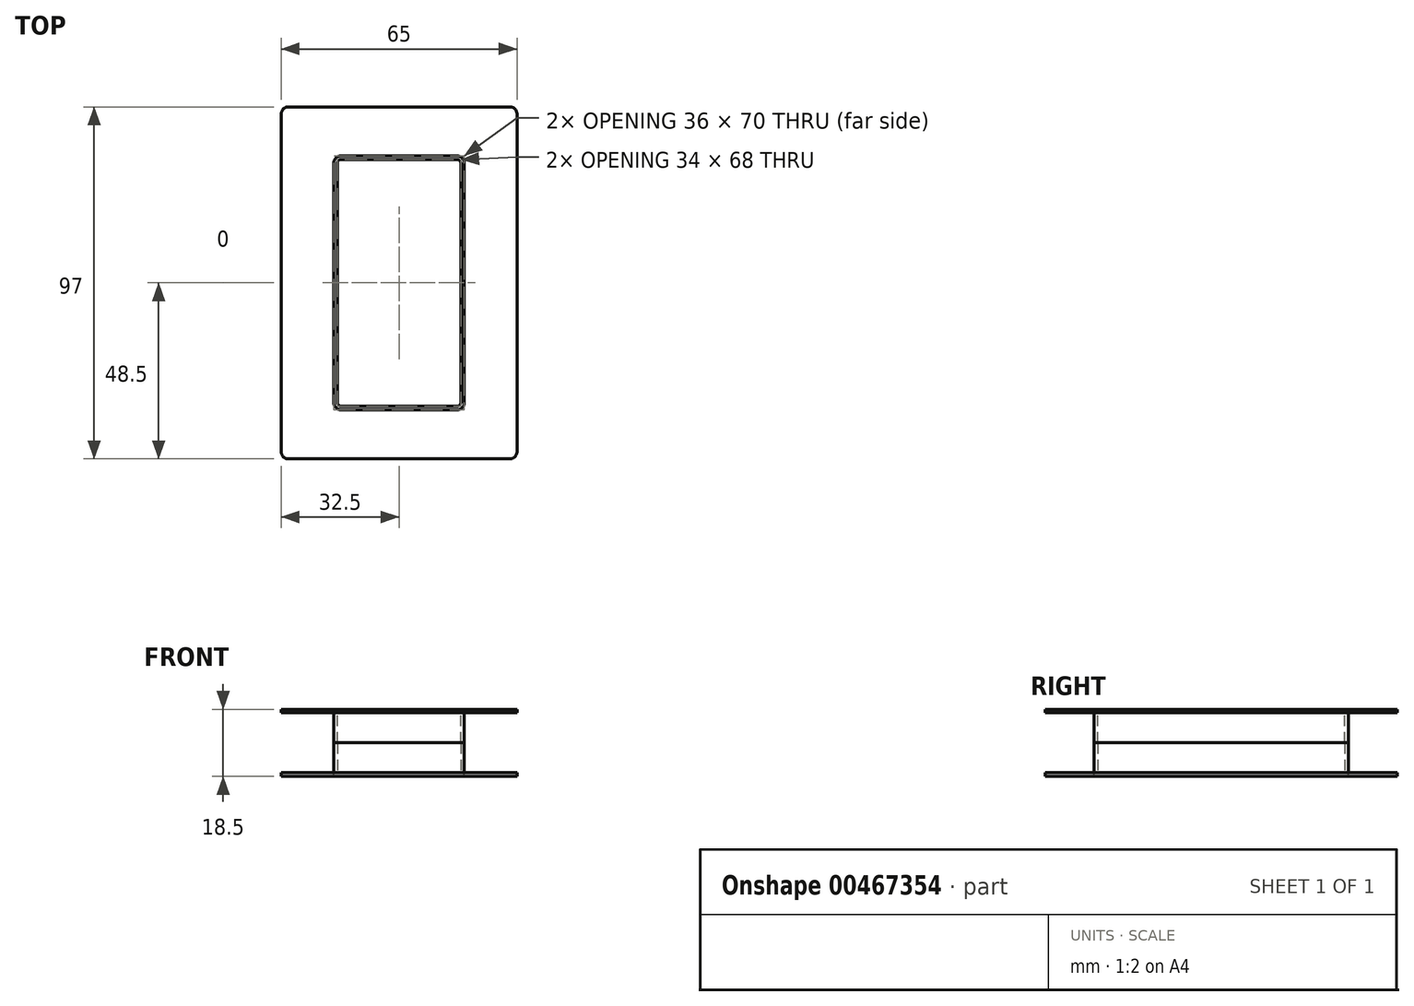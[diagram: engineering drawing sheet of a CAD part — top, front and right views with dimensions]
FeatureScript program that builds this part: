
annotation { "Feature Type Name" : "Feature", "Feature Type Description" : "" }
export const myFeature = defineFeature(function(context is Context, id is Id, definition is map)
    precondition{}
    {
        {
            var Q0;
            Q0=qCreatedBy(makeId("Top.planeOp"),FACE);
            var sketch = newSketch(context, id + "F0", { "sketchPlane" : qUnion([Q0])});
            skLineSegment(sketch, "E0.bottom", {"start": v(-16, -33) * mm, "end": v(16, -33) * mm, "construction": true});
            skLineSegment(sketch, "E0.top", {"start": v(-16, 33) * mm, "end": v(16, 33) * mm, "construction": true});
            skLineSegment(sketch, "E0.left", {"start": v(-16, -33) * mm, "end": v(-16, 33) * mm, "construction": true});
            skLineSegment(sketch, "E0.right", {"start": v(16, -33) * mm, "end": v(16, 33) * mm, "construction": true});
            skPoint(sketch, "E0.middle", {"position": v(0, 0) * mm});
            skLineSegment(sketch, "E1.bottom", {"start": v(33, -33) * mm, "end": v(65, -33) * mm, "construction": true});
            skLineSegment(sketch, "E1.top", {"start": v(33, 33) * mm, "end": v(65, 33) * mm, "construction": true});
            skLineSegment(sketch, "E1.left", {"start": v(33, -33) * mm, "end": v(33, 33) * mm, "construction": true});
            skLineSegment(sketch, "E1.right", {"start": v(65, -33) * mm, "end": v(65, 33) * mm, "construction": true});
            skLineSegment(sketch, "E2", {"start": v(33, 33) * mm, "end": v(16, 33) * mm, "construction": true});
            skLineSegment(sketch, "E3.MirrorCS", {"start": v(-33, 33) * mm, "end": v(-65, 33) * mm, "construction": true});
            skLineSegment(sketch, "E4.MirrorCS", {"start": v(-33, -33) * mm, "end": v(-65, -33) * mm, "construction": true});
            skLineSegment(sketch, "E5.MirrorCS", {"start": v(-33, -33) * mm, "end": v(-33, 33) * mm, "construction": true});
            skLineSegment(sketch, "E6.MirrorCS", {"start": v(-65, -33) * mm, "end": v(-65, 33) * mm, "construction": true});
            skArc(sketch, "E7", {"start": v(17, 33) * mm, "mid": v(16.7, 33.7) * mm, "end": v(16, 34) * mm});
            skArc(sketch, "E8.MirrorCS", {"start": v(-17, 33) * mm, "mid": v(-16.7, 33.7) * mm, "end": v(-16, 34) * mm});
            skArc(sketch, "E9.MirrorCS", {"start": v(-17, -33) * mm, "mid": v(-16.7, -33.7) * mm, "end": v(-16, -34) * mm});
            skArc(sketch, "E10.MirrorCS", {"start": v(17, -33) * mm, "mid": v(16.7, -33.7) * mm, "end": v(16, -34) * mm});
            skLineSegment(sketch, "E11", {"start": v(-16, 34) * mm, "end": v(16, 34) * mm});
            skLineSegment(sketch, "E12", {"start": v(17, 33) * mm, "end": v(17, -33) * mm});
            skLineSegment(sketch, "E13", {"start": v(16, -34) * mm, "end": v(-16, -34) * mm});
            skLineSegment(sketch, "E14", {"start": v(-17, -33) * mm, "end": v(-17, 33) * mm});
            skLineSegment(sketch, "E15", {"start": v(33, 0) * mm, "end": v(32.5, 0) * mm, "construction": true});
            skPoint(sketch, "E15.endSnap0", {"position": v(33, 0) * mm});
            skLineSegment(sketch, "E16", {"start": v(32.5, 0) * mm, "end": v(32.5, 46.5) * mm});
            skLineSegment(sketch, "E17.MirrorCS", {"start": v(32.5, 0) * mm, "end": v(32.5, -46.5) * mm});
            skLineSegment(sketch, "E18", {"start": v(32.5, 0) * mm, "end": v(17, 0) * mm, "construction": true});
            skLineSegment(sketch, "E19", {"start": v(0, 33) * mm, "end": v(0, 48.5) * mm, "construction": true});
            skPoint(sketch, "E19.endSnap0", {"position": v(0, 33) * mm});
            skLineSegment(sketch, "E20", {"start": v(0, 48.5) * mm, "end": v(30.5, 48.5) * mm});
            skLineSegment(sketch, "E21.MirrorCS", {"start": v(0, 48.5) * mm, "end": v(-30.5, 48.5) * mm});
            skLineSegment(sketch, "E22.MirrorCS", {"start": v(0, -48.5) * mm, "end": v(30.5, -48.5) * mm});
            skLineSegment(sketch, "E23.MirrorCS", {"start": v(0, -48.5) * mm, "end": v(-30.5, -48.5) * mm});
            skLineSegment(sketch, "E24.MirrorCS", {"start": v(-32.5, 0) * mm, "end": v(-32.5, 46.5) * mm});
            skLineSegment(sketch, "E25.MirrorCS", {"start": v(-32.5, 0) * mm, "end": v(-32.5, -46.5) * mm});
            skPoint(sketch, "E26.visualSharp", {"position": v(32.5, 48.5) * mm});
            skArc(sketch, "E26.filletArc", {"start": v(32.5, 46.5) * mm, "mid": v(31.91, 47.91) * mm, "end": v(30.5, 48.5) * mm});
            skPoint(sketch, "E27.visualSharp", {"position": v(-32.5, 48.5) * mm});
            skArc(sketch, "E27.filletArc", {"start": v(-30.5, 48.5) * mm, "mid": v(-31.91, 47.91) * mm, "end": v(-32.5, 46.5) * mm});
            skPoint(sketch, "E28.visualSharp", {"position": v(-32.5, -48.5) * mm});
            skArc(sketch, "E28.filletArc", {"start": v(-32.5, -46.5) * mm, "mid": v(-31.91, -47.91) * mm, "end": v(-30.5, -48.5) * mm});
            skPoint(sketch, "E29.visualSharp", {"position": v(32.5, -48.5) * mm});
            skArc(sketch, "E29.filletArc", {"start": v(30.5, -48.5) * mm, "mid": v(31.91, -47.91) * mm, "end": v(32.5, -46.5) * mm});
            skLineSegment(sketch, "E30", {"start": v(18, 33) * mm, "end": v(18, -33) * mm});
            skLineSegment(sketch, "E31.MirrorCS", {"start": v(-18, 33) * mm, "end": v(-18, -33) * mm});
            skLineSegment(sketch, "E32", {"start": v(-16, 35) * mm, "end": v(16, 35) * mm});
            skLineSegment(sketch, "E33", {"start": v(-16, 34) * mm, "end": v(-16, 35) * mm, "construction": true});
            skLineSegment(sketch, "E34.MirrorCS", {"start": v(-16, -35) * mm, "end": v(16, -35) * mm});
            skArc(sketch, "E35", {"start": v(-18, 33) * mm, "mid": v(-17.41, 34.41) * mm, "end": v(-16, 35) * mm});
            skArc(sketch, "E36", {"start": v(16, 35) * mm, "mid": v(17.41, 34.41) * mm, "end": v(18, 33) * mm});
            skArc(sketch, "E37", {"start": v(-18, -33) * mm, "mid": v(-17.41, -34.41) * mm, "end": v(-16, -35) * mm});
            skArc(sketch, "E38", {"start": v(18, -33) * mm, "mid": v(17.41, -34.41) * mm, "end": v(16, -35) * mm});
            skSolve(sketch);
        }
        {
            var Q0;
            Q0=makeQuery(id+"F0.imprint","IMPRINT",FACE,{"disambiguationData":[TD([[makeQuery(id+"F0.imprint","IMPRINT",EDGE,{"derivedFrom":sQuery(id+"F0.wireOp",EDGE,"E16")}),1.0]])]});
            extrude(context, id + "F1", {"entities" : qUnion([Q0]), "depth" : 1 * mm});
        }
        {
            var Q0;
            Q0=makeQuery(id+"F0.imprint","IMPRINT",FACE,{"disambiguationData":[TD([[makeQuery(id+"F0.imprint","IMPRINT",EDGE,{"derivedFrom":sQuery(id+"F0.wireOp",EDGE,"E7")}),-1.0]])]});
            extrude(context, id + "F2", {"entities" : qUnion([Q0]), "oppositeDirection" : true, "depth" : 8.25 * mm});
        }
        {
            var Q0;
            Q0=qCreatedBy(makeId("Top.planeOp"),FACE);
            cPlane(context, id + "F3", {"entities" : qUnion([Q0]), "cplaneType" : CPlaneType.OFFSET, "offset" : 8.25 * mm, "oppositeDirection" : true, "width" : 150 * mm, "height" : 150 * mm});
        }
        {
            var Q0;
            Q0=makeQuery(id+"F1.opExtrude","SWEPT_BODY",BODY,{"disambiguationData":[OSD([sQuery(id+"F0.wireOp",EDGE,"E16"),sQuery(id+"F0.wireOp",EDGE,"E17.MirrorCS"),sQuery(id+"F0.wireOp",EDGE,"E20"),sQuery(id+"F0.wireOp",EDGE,"E21.MirrorCS"),sQuery(id+"F0.wireOp",EDGE,"E22.MirrorCS"),sQuery(id+"F0.wireOp",EDGE,"E23.MirrorCS"),sQuery(id+"F0.wireOp",EDGE,"E24.MirrorCS"),sQuery(id+"F0.wireOp",EDGE,"E25.MirrorCS"),sQuery(id+"F0.wireOp",EDGE,"E26.filletArc"),sQuery(id+"F0.wireOp",EDGE,"E27.filletArc"),sQuery(id+"F0.wireOp",EDGE,"E28.filletArc"),sQuery(id+"F0.wireOp",EDGE,"E29.filletArc"),sQuery(id+"F0.wireOp",EDGE,"E30"),sQuery(id+"F0.wireOp",EDGE,"E31.MirrorCS"),sQuery(id+"F0.wireOp",EDGE,"E32"),sQuery(id+"F0.wireOp",EDGE,"E34.MirrorCS"),sQuery(id+"F0.wireOp",EDGE,"E35"),sQuery(id+"F0.wireOp",EDGE,"E36"),sQuery(id+"F0.wireOp",EDGE,"E37"),sQuery(id+"F0.wireOp",EDGE,"E38")])]});
            var Q1;
            Q1=makeQuery(id+"F2.opExtrude","SWEPT_BODY",BODY,{"disambiguationData":[OSD([sQuery(id+"F0.wireOp",EDGE,"E7"),sQuery(id+"F0.wireOp",EDGE,"E8.MirrorCS"),sQuery(id+"F0.wireOp",EDGE,"E9.MirrorCS"),sQuery(id+"F0.wireOp",EDGE,"E10.MirrorCS"),sQuery(id+"F0.wireOp",EDGE,"E11"),sQuery(id+"F0.wireOp",EDGE,"E12"),sQuery(id+"F0.wireOp",EDGE,"E13"),sQuery(id+"F0.wireOp",EDGE,"E14"),sQuery(id+"F0.wireOp",EDGE,"E30"),sQuery(id+"F0.wireOp",EDGE,"E31.MirrorCS"),sQuery(id+"F0.wireOp",EDGE,"E32"),sQuery(id+"F0.wireOp",EDGE,"E34.MirrorCS"),sQuery(id+"F0.wireOp",EDGE,"E35"),sQuery(id+"F0.wireOp",EDGE,"E36"),sQuery(id+"F0.wireOp",EDGE,"E37"),sQuery(id+"F0.wireOp",EDGE,"E38")])]});
            var Q2;
            Q2=qCreatedBy(id+"F3.planeOp",FACE);
            mirror(context, id + "F4", {"entities" : qUnion([Q0, Q1]), "mirrorPlane" : qUnion([Q2])});
        }
    });
